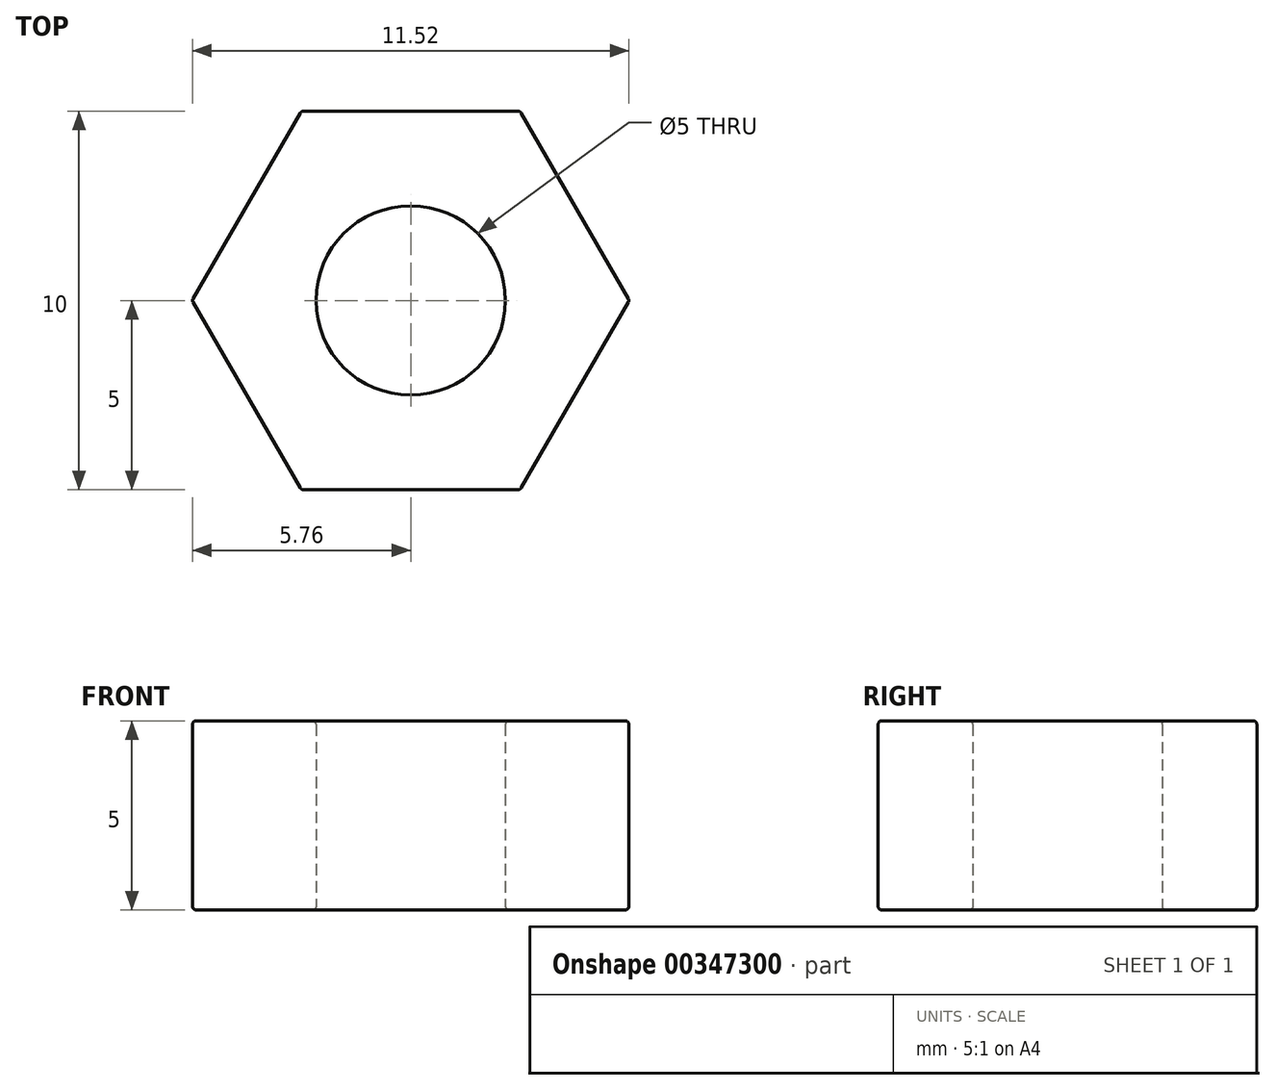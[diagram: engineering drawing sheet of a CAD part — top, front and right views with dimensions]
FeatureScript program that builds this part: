
annotation { "Feature Type Name" : "Feature", "Feature Type Description" : "" }
export const myFeature = defineFeature(function(context is Context, id is Id, definition is map)
    precondition{}
    {
        {
            var Q0;
            Q0=qCreatedBy(makeId("Top.planeOp"),FACE);
            var sketch = newSketch(context, id + "F0", { "sketchPlane" : qUnion([Q0])});
            skCircle(sketch, "E0.cCircle", {"center": v(0, 0) * mm, "radius": 5 * mm, "construction": true});
            skLineSegment(sketch, "E0.0", {"start": v(2.89, -5) * mm, "end": v(-2.89, -5) * mm});
            skLineSegment(sketch, "E0.1", {"start": v(-2.89, -5) * mm, "end": v(-5.77, 0) * mm});
            skLineSegment(sketch, "E0.2", {"start": v(-5.77, 0) * mm, "end": v(-2.89, 5) * mm});
            skLineSegment(sketch, "E0.3", {"start": v(-2.89, 5) * mm, "end": v(2.89, 5) * mm});
            skLineSegment(sketch, "E0.4", {"start": v(2.89, 5) * mm, "end": v(5.77, 0) * mm});
            skLineSegment(sketch, "E0.5", {"start": v(5.77, 0) * mm, "end": v(2.89, -5) * mm});
            skPoint(sketch, "E0.0.midPoint", {"position": v(0, -5) * mm});
            skCircle(sketch, "E1", {"center": v(0, 0) * mm, "radius": 2.5 * mm});
            skSolve(sketch);
        }
        {
            var Q0;
            Q0 = qSketchRegion(id + "F0", true);
            extrude(context, id + "F1", {"entities" : qUnion([Q0]), "depth" : 5 * mm});
        }
        {
            var Q0;
            Q0=makeQuery(id+"F1.opExtrude","SWEPT_EDGE",EDGE,{"disambiguationData":[OSD([sQuery(id+"F0.wireOp",EDGE,"E0.0"),sQuery(id+"F0.wireOp",EDGE,"E0.5")])]});
            var Q1;
            Q1=makeQuery(id+"F1.opExtrude","SWEPT_EDGE",EDGE,{"disambiguationData":[OSD([sQuery(id+"F0.wireOp",EDGE,"E0.4"),sQuery(id+"F0.wireOp",EDGE,"E0.5")])]});
            var Q2;
            Q2=makeQuery(id+"F1.opExtrude","SWEPT_EDGE",EDGE,{"disambiguationData":[OSD([sQuery(id+"F0.wireOp",EDGE,"E0.3"),sQuery(id+"F0.wireOp",EDGE,"E0.4")])]});
            var Q3;
            Q3=makeQuery(id+"F1.opExtrude","SWEPT_FACE",FACE,{"disambiguationData":[OSD([sQuery(id+"F0.wireOp",EDGE,"E1")])]});
            var Q4;
            Q4=makeQuery(id+"F1.opExtrude","CAP_EDGE",EDGE,{"disambiguationData":[OSD([sQuery(id+"F0.wireOp",EDGE,"E0.0")])],"isStart":false});
            var Q5;
            Q5=makeQuery(id+"F1.opExtrude","SWEPT_FACE",FACE,{"disambiguationData":[OSD([sQuery(id+"F0.wireOp",EDGE,"E0.0")])]});
            var Q6;
            Q6=makeQuery(id+"F1.opExtrude","CAP_FACE",FACE,{"disambiguationData":[OSD([sQuery(id+"F0.wireOp",EDGE,"E0.0"),sQuery(id+"F0.wireOp",EDGE,"E0.1"),sQuery(id+"F0.wireOp",EDGE,"E0.2"),sQuery(id+"F0.wireOp",EDGE,"E0.3"),sQuery(id+"F0.wireOp",EDGE,"E0.4"),sQuery(id+"F0.wireOp",EDGE,"E0.5"),sQuery(id+"F0.wireOp",EDGE,"E1")])],"isStart":false});
            var Q7;
            Q7=makeQuery(id+"F1.opExtrude","SWEPT_FACE",FACE,{"disambiguationData":[OSD([sQuery(id+"F0.wireOp",EDGE,"E0.2")])]});
            var Q8;
            Q8=makeQuery(id+"F1.opExtrude","SWEPT_FACE",FACE,{"disambiguationData":[OSD([sQuery(id+"F0.wireOp",EDGE,"E0.3")])]});
            var Q9;
            Q9=makeQuery(id+"F1.opExtrude","CAP_FACE",FACE,{"disambiguationData":[OSD([sQuery(id+"F0.wireOp",EDGE,"E0.0"),sQuery(id+"F0.wireOp",EDGE,"E0.1"),sQuery(id+"F0.wireOp",EDGE,"E0.2"),sQuery(id+"F0.wireOp",EDGE,"E0.3"),sQuery(id+"F0.wireOp",EDGE,"E0.4"),sQuery(id+"F0.wireOp",EDGE,"E0.5"),sQuery(id+"F0.wireOp",EDGE,"E1")])],"isStart":true});
            fillet(context, id + "F2", {"entities" : qUnion([Q0, Q1, Q2, Q3, Q4, Q5, Q6, Q7, Q8, Q9]), "radius" : 0.1 * mm, "tangentPropagation" : true, "allowEdgeOverflow" : false});
        }
    });
